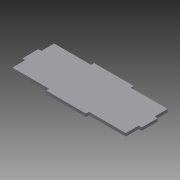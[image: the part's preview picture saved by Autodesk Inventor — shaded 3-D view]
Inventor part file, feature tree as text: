
AUTODESK INVENTOR PART (.ipt)
format: ipt  version: 2013 (Build 170138000, 138)  size: 101,888 bytes
history: native  units: in
note: dims shown in document units (in); Inventor stores cm internally (conversion verified against a paired STEP export)
features: extrude x2, sketch x2
ambient origin geometry x8: Origin, YZ Plane, XZ Plane, XY Plane, X Axis, Y Axis, Z Axis, Center Point
bodies: Solid1 (feature_tree)
feature tree (4):
  extrude  "Extrusion1"  Depth=1.75in
  extrude  "Extrusion2"  TaperAngle=0.0deg  [1 undecoded]
  sketch  "Sketch1"  dims[d0=4.75in d1=1.75in]
  sketch  "Sketch2"  dims[d2=0.125in d3=0.0in d4=1.6667in d5=0.125in d6=1.5417in d7=1.6667in d8=0.125in d9=0.125in d10=0.6667in d11=0.125in d12=0.6667in d13=0.5417in d14=0.125in d15=0.0in]
note: 1 required parameter value undecoded (feature->parameter linkage not recoverable at this tier; creation-order binding heuristic only, values carry confidence <= 0.55)
